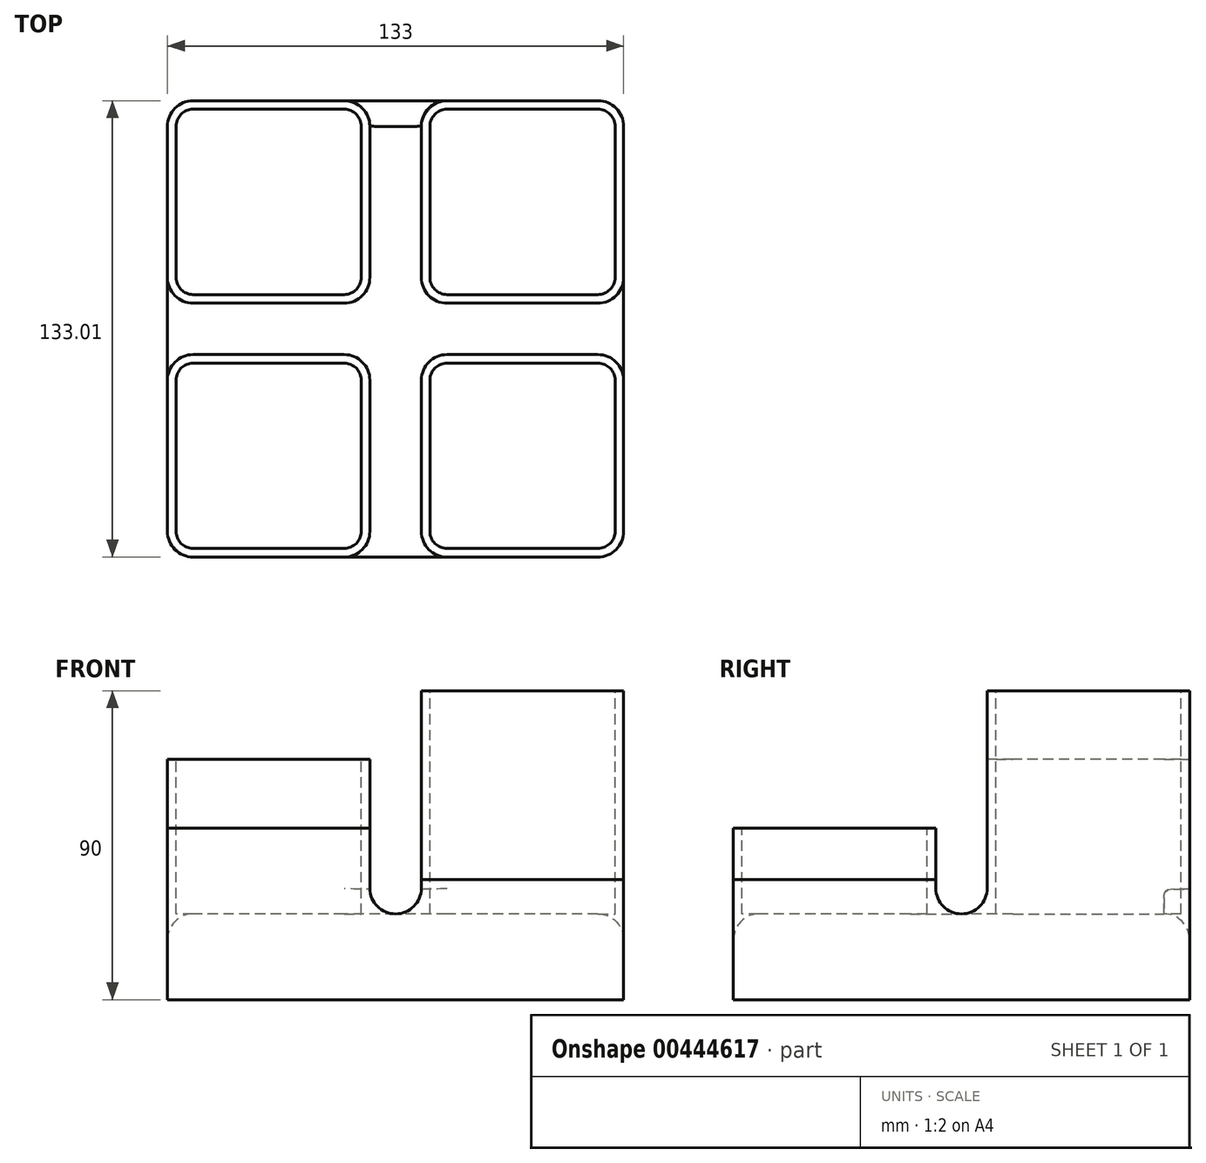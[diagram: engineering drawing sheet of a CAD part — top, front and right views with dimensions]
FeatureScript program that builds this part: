
annotation { "Feature Type Name" : "Feature", "Feature Type Description" : "" }
export const myFeature = defineFeature(function(context is Context, id is Id, definition is map)
    precondition{}
    {
        {
            var Q0;
            Q0=qCreatedBy(makeId("Top.planeOp"),FACE);
            var sketch = newSketch(context, id + "F0", { "sketchPlane" : qUnion([Q0])});
            skLineSegment(sketch, "E0", {"start": v(-66.5, 59) * mm, "end": v(-66.5, 15) * mm});
            skLineSegment(sketch, "E1", {"start": v(-15, -66.5) * mm, "end": v(-59, -66.5) * mm});
            skLineSegment(sketch, "E2", {"start": v(-66.5, -59) * mm, "end": v(-66.5, -15) * mm});
            skLineSegment(sketch, "E3", {"start": v(59, -66.5) * mm, "end": v(15, -66.5) * mm});
            skLineSegment(sketch, "E4", {"start": v(-59, -7.5) * mm, "end": v(-15, -7.5) * mm});
            skLineSegment(sketch, "E5", {"start": v(-7.5, -15) * mm, "end": v(-7.5, -59) * mm});
            skLineSegment(sketch, "E6", {"start": v(-59, 66.5) * mm, "end": v(-15, 66.5) * mm});
            skLineSegment(sketch, "E7", {"start": v(-7.5, 59) * mm, "end": v(-7.5, 15) * mm});
            skLineSegment(sketch, "E8", {"start": v(-15, 7.5) * mm, "end": v(-59, 7.5) * mm});
            skLineSegment(sketch, "E9", {"start": v(66.5, 59) * mm, "end": v(66.5, 15) * mm});
            skLineSegment(sketch, "E10", {"start": v(59, 7.5) * mm, "end": v(15, 7.5) * mm});
            skLineSegment(sketch, "E11", {"start": v(7.5, 15) * mm, "end": v(7.5, 59) * mm});
            skLineSegment(sketch, "E12", {"start": v(15, 66.5) * mm, "end": v(59, 66.5) * mm});
            skLineSegment(sketch, "E13", {"start": v(66.5, -59) * mm, "end": v(66.5, -15) * mm});
            skLineSegment(sketch, "E14", {"start": v(59, -7.5) * mm, "end": v(15, -7.5) * mm});
            skLineSegment(sketch, "E15", {"start": v(7.5, -15) * mm, "end": v(7.5, -59) * mm});
            skPoint(sketch, "E16.visualSharp", {"position": v(-64, 64) * mm});
            skPoint(sketch, "E17.visualSharp", {"position": v(-66.5, 66.5) * mm});
            skArc(sketch, "E17.filletArc", {"start": v(-59, 66.5) * mm, "mid": v(-64.3, 64.3) * mm, "end": v(-66.5, 59) * mm});
            skPoint(sketch, "E18.visualSharp", {"position": v(-64, 10) * mm});
            skPoint(sketch, "E19.newPointB", {"position": v(-66.5, 7.5) * mm});
            skArc(sketch, "E19.filletArc", {"start": v(-66.5, 15) * mm, "mid": v(-64.3, 9.7) * mm, "end": v(-59, 7.5) * mm});
            skPoint(sketch, "E20.visualSharp", {"position": v(-7.5, 7.5) * mm});
            skArc(sketch, "E20.filletArc", {"start": v(-15, 7.5) * mm, "mid": v(-9.7, 9.7) * mm, "end": v(-7.5, 15) * mm});
            skPoint(sketch, "E21.visualSharp", {"position": v(-10, 10) * mm});
            skPoint(sketch, "E22.visualSharp", {"position": v(-10, 64) * mm});
            skPoint(sketch, "E23.visualSharp", {"position": v(-7.5, 66.5) * mm});
            skArc(sketch, "E23.filletArc", {"start": v(-7.5, 59) * mm, "mid": v(-9.7, 64.3) * mm, "end": v(-15, 66.5) * mm});
            skPoint(sketch, "E24.visualSharp", {"position": v(10, 64) * mm});
            skPoint(sketch, "E25.visualSharp", {"position": v(7.5, 66.5) * mm});
            skArc(sketch, "E25.filletArc", {"start": v(15, 66.5) * mm, "mid": v(9.7, 64.3) * mm, "end": v(7.5, 59) * mm});
            skPoint(sketch, "E26.visualSharp", {"position": v(66.5, 66.5) * mm});
            skArc(sketch, "E26.filletArc", {"start": v(66.5, 59) * mm, "mid": v(64.3, 64.3) * mm, "end": v(59, 66.5) * mm});
            skPoint(sketch, "E27.visualSharp", {"position": v(64, 64) * mm});
            skPoint(sketch, "E28.visualSharp", {"position": v(66.5, -7.5) * mm});
            skArc(sketch, "E28.filletArc", {"start": v(66.5, -15) * mm, "mid": v(64.3, -9.7) * mm, "end": v(59, -7.5) * mm});
            skPoint(sketch, "E29.visualSharp", {"position": v(64, -10) * mm});
            skPoint(sketch, "E30.visualSharp", {"position": v(10, -10) * mm});
            skPoint(sketch, "E31.visualSharp", {"position": v(7.5, -7.5) * mm});
            skArc(sketch, "E31.filletArc", {"start": v(15, -7.5) * mm, "mid": v(9.7, -9.7) * mm, "end": v(7.5, -15) * mm});
            skPoint(sketch, "E32.visualSharp", {"position": v(10, -64) * mm});
            skArc(sketch, "E33.filletArc", {"start": v(7.5, -59) * mm, "mid": v(9.7, -64.3) * mm, "end": v(15, -66.5) * mm});
            skPoint(sketch, "E34.visualSharp", {"position": v(64, -64) * mm});
            skPoint(sketch, "E35.visualSharp", {"position": v(66.5, -66.5) * mm});
            skArc(sketch, "E35.filletArc", {"start": v(59, -66.5) * mm, "mid": v(64.3, -64.3) * mm, "end": v(66.5, -59) * mm});
            skPoint(sketch, "E36.visualSharp", {"position": v(10, 10) * mm});
            skPoint(sketch, "E37.visualSharp", {"position": v(7.5, 7.5) * mm});
            skArc(sketch, "E37.filletArc", {"start": v(7.5, 15) * mm, "mid": v(9.7, 9.7) * mm, "end": v(15, 7.5) * mm});
            skPoint(sketch, "E38.visualSharp", {"position": v(64, 10) * mm});
            skArc(sketch, "E39.filletArc", {"start": v(59, 7.5) * mm, "mid": v(64.3, 9.7) * mm, "end": v(66.5, 15) * mm});
            skPoint(sketch, "E40.visualSharp", {"position": v(-64, -10) * mm});
            skArc(sketch, "E41.filletArc", {"start": v(-59, -7.5) * mm, "mid": v(-64.3, -9.7) * mm, "end": v(-66.5, -15) * mm});
            skPoint(sketch, "E42.visualSharp", {"position": v(-64, -64) * mm});
            skPoint(sketch, "E43.visualSharp", {"position": v(-66.5, -66.5) * mm});
            skArc(sketch, "E43.filletArc", {"start": v(-66.5, -59) * mm, "mid": v(-64.3, -64.3) * mm, "end": v(-59, -66.5) * mm});
            skPoint(sketch, "E44.visualSharp", {"position": v(-7.5, -7.5) * mm});
            skArc(sketch, "E44.filletArc", {"start": v(-7.5, -15) * mm, "mid": v(-9.7, -9.7) * mm, "end": v(-15, -7.5) * mm});
            skPoint(sketch, "E45.visualSharp", {"position": v(-10, -10) * mm});
            skPoint(sketch, "E46.visualSharp", {"position": v(-10, -64) * mm});
            skPoint(sketch, "E47.visualSharp", {"position": v(-7.5, -66.5) * mm});
            skArc(sketch, "E47.filletArc", {"start": v(-15, -66.5) * mm, "mid": v(-9.7, -64.3) * mm, "end": v(-7.5, -59) * mm});
            skPoint(sketch, "E48.trimOffspring.end.orphan", {"position": v(-66.5, 0) * mm});
            skPoint(sketch, "E49.orphan", {"position": v(66.5, 7.5) * mm});
            skSolve(sketch);
        }
        {
            var Q0;
            Q0=makeQuery(id+"F0.imprint","IMPRINT",FACE,{"disambiguationData":[TD([[makeQuery(id+"F0.imprint","IMPRINT",EDGE,{"derivedFrom":sQuery(id+"F0.wireOp",EDGE,"E0")}),1.0]])]});
            extrude(context, id + "F1", {"entities" : qUnion([Q0]), "depth" : 70 * mm});
        }
        {
            var Q0;
            Q0=makeQuery(id+"F0.imprint","IMPRINT",FACE,{"disambiguationData":[TD([[makeQuery(id+"F0.imprint","IMPRINT",EDGE,{"derivedFrom":sQuery(id+"F0.wireOp",EDGE,"E9")}),-1.0]])]});
            extrude(context, id + "F2", {"entities" : qUnion([Q0]), "depth" : 90 * mm});
        }
        {
            var Q0;
            Q0=makeQuery(id+"F0.imprint","IMPRINT",FACE,{"disambiguationData":[TD([[makeQuery(id+"F0.imprint","IMPRINT",EDGE,{"derivedFrom":sQuery(id+"F0.wireOp",EDGE,"E2")}),-1.0]])]});
            extrude(context, id + "F3", {"entities" : qUnion([Q0]), "depth" : 50 * mm});
        }
        {
            var Q0;
            Q0=makeQuery(id+"F0.imprint","IMPRINT",FACE,{"disambiguationData":[TD([[makeQuery(id+"F0.imprint","IMPRINT",EDGE,{"derivedFrom":sQuery(id+"F0.wireOp",EDGE,"E3")}),-1.0]])]});
            extrude(context, id + "F4", {"entities" : qUnion([Q0]), "depth" : 35 * mm});
        }
        {
            var Q0;
            Q0=makeQuery(id+"F1.opExtrude","CAP_FACE",FACE,{"disambiguationData":[OSD([sQuery(id+"F0.wireOp",EDGE,"E0"),sQuery(id+"F0.wireOp",EDGE,"E6"),sQuery(id+"F0.wireOp",EDGE,"E7"),sQuery(id+"F0.wireOp",EDGE,"E8"),sQuery(id+"F0.wireOp",EDGE,"E17.filletArc"),sQuery(id+"F0.wireOp",EDGE,"E19.filletArc"),sQuery(id+"F0.wireOp",EDGE,"E20.filletArc"),sQuery(id+"F0.wireOp",EDGE,"E23.filletArc")])],"isStart":false});
            var sketch = newSketch(context, id + "F5", { "sketchPlane" : qUnion([Q0])});
            skArc(sketch, "E50.0", {"start": v(-59, 64) * mm, "mid": v(-62.54, 62.54) * mm, "end": v(-64, 59) * mm});
            skLineSegment(sketch, "E50.1", {"start": v(-64, 59) * mm, "end": v(-64, 15) * mm});
            skLineSegment(sketch, "E50.2", {"start": v(-59, 64) * mm, "end": v(-15, 64) * mm});
            skArc(sketch, "E50.3", {"start": v(-64, 15) * mm, "mid": v(-62.54, 11.46) * mm, "end": v(-59, 10) * mm});
            skArc(sketch, "E50.4", {"start": v(-10, 59) * mm, "mid": v(-11.46, 62.54) * mm, "end": v(-15, 64) * mm});
            skLineSegment(sketch, "E50.5", {"start": v(-10, 59) * mm, "end": v(-10, 15) * mm});
            skArc(sketch, "E50.6", {"start": v(-15, 10) * mm, "mid": v(-11.46, 11.46) * mm, "end": v(-10, 15) * mm});
            skLineSegment(sketch, "E50.7", {"start": v(-15, 10) * mm, "end": v(-59, 10) * mm});
            skSolve(sketch);
        }
        {
            var Q0;
            Q0=makeQuery(id+"F5.imprint","IMPRINT",FACE,{"disambiguationData":[TD([[makeQuery(id+"F5.imprint","IMPRINT",EDGE,{"derivedFrom":sQuery(id+"F5.wireOp",EDGE,"E50.0")}),1.0]])]});
            extrude(context, id + "F6", {"entities" : qUnion([Q0]), "operationType" : NewBodyOperationType.REMOVE, "endBound" : BoundingType.THROUGH_ALL, "oppositeDirection" : true, "depth" : 25 * mm});
        }
        {
            var Q0;
            Q0=makeQuery(id+"F2.opExtrude","CAP_FACE",FACE,{"disambiguationData":[OSD([sQuery(id+"F0.wireOp",EDGE,"E9"),sQuery(id+"F0.wireOp",EDGE,"E10"),sQuery(id+"F0.wireOp",EDGE,"E11"),sQuery(id+"F0.wireOp",EDGE,"E12"),sQuery(id+"F0.wireOp",EDGE,"E25.filletArc"),sQuery(id+"F0.wireOp",EDGE,"E26.filletArc"),sQuery(id+"F0.wireOp",EDGE,"E37.filletArc"),sQuery(id+"F0.wireOp",EDGE,"E39.filletArc")])],"isStart":false});
            var sketch = newSketch(context, id + "F7", { "sketchPlane" : qUnion([Q0])});
            skArc(sketch, "E51.0", {"start": v(15, 64) * mm, "mid": v(11.46, 62.54) * mm, "end": v(10, 59) * mm});
            skLineSegment(sketch, "E51.1", {"start": v(10, 15) * mm, "end": v(10, 59) * mm});
            skLineSegment(sketch, "E51.2", {"start": v(15, 64) * mm, "end": v(59, 64) * mm});
            skArc(sketch, "E51.3", {"start": v(10, 15) * mm, "mid": v(11.46, 11.46) * mm, "end": v(15, 10) * mm});
            skArc(sketch, "E51.4", {"start": v(64, 59) * mm, "mid": v(62.54, 62.54) * mm, "end": v(59, 64) * mm});
            skLineSegment(sketch, "E51.5", {"start": v(64, 59) * mm, "end": v(64, 15) * mm});
            skArc(sketch, "E51.6", {"start": v(59, 10) * mm, "mid": v(62.54, 11.46) * mm, "end": v(64, 15) * mm});
            skLineSegment(sketch, "E51.7", {"start": v(59, 10) * mm, "end": v(15, 10) * mm});
            skSolve(sketch);
        }
        {
            var Q0;
            Q0=makeQuery(id+"F7.imprint","IMPRINT",FACE,{"disambiguationData":[TD([[makeQuery(id+"F7.imprint","IMPRINT",EDGE,{"derivedFrom":sQuery(id+"F7.wireOp",EDGE,"E51.0")}),1.0]])]});
            extrude(context, id + "F8", {"entities" : qUnion([Q0]), "operationType" : NewBodyOperationType.REMOVE, "endBound" : BoundingType.THROUGH_ALL, "oppositeDirection" : true, "depth" : 25 * mm});
        }
        {
            var Q0;
            Q0=makeQuery(id+"F3.opExtrude","CAP_FACE",FACE,{"disambiguationData":[OSD([sQuery(id+"F0.wireOp",EDGE,"E2"),sQuery(id+"F0.wireOp",EDGE,"E4"),sQuery(id+"F0.wireOp",EDGE,"E5"),sQuery(id+"F0.wireOp",EDGE,"E1"),sQuery(id+"F0.wireOp",EDGE,"E41.filletArc"),sQuery(id+"F0.wireOp",EDGE,"E43.filletArc"),sQuery(id+"F0.wireOp",EDGE,"E44.filletArc"),sQuery(id+"F0.wireOp",EDGE,"E47.filletArc")])],"isStart":false});
            var sketch = newSketch(context, id + "F9", { "sketchPlane" : qUnion([Q0])});
            skArc(sketch, "E52.0", {"start": v(-59, -10) * mm, "mid": v(-62.54, -11.46) * mm, "end": v(-64, -15) * mm});
            skLineSegment(sketch, "E52.1", {"start": v(-64, -59) * mm, "end": v(-64, -15) * mm});
            skLineSegment(sketch, "E52.2", {"start": v(-59, -10) * mm, "end": v(-15, -10) * mm});
            skArc(sketch, "E52.3", {"start": v(-64, -59) * mm, "mid": v(-62.54, -62.54) * mm, "end": v(-59, -64) * mm});
            skArc(sketch, "E52.4", {"start": v(-10, -15) * mm, "mid": v(-11.46, -11.46) * mm, "end": v(-15, -10) * mm});
            skLineSegment(sketch, "E52.5", {"start": v(-10, -15) * mm, "end": v(-10, -59) * mm});
            skArc(sketch, "E52.6", {"start": v(-15, -64) * mm, "mid": v(-11.46, -62.54) * mm, "end": v(-10, -59) * mm});
            skLineSegment(sketch, "E52.7", {"start": v(-15, -64) * mm, "end": v(-59, -64) * mm});
            skSolve(sketch);
        }
        {
            var Q0;
            Q0=makeQuery(id+"F9.imprint","IMPRINT",FACE,{"disambiguationData":[TD([[makeQuery(id+"F9.imprint","IMPRINT",EDGE,{"derivedFrom":sQuery(id+"F9.wireOp",EDGE,"E52.0")}),1.0]])]});
            extrude(context, id + "F10", {"entities" : qUnion([Q0]), "operationType" : NewBodyOperationType.REMOVE, "endBound" : BoundingType.THROUGH_ALL, "oppositeDirection" : true, "depth" : 25 * mm});
        }
        {
            var Q0;
            Q0=makeQuery(id+"F4.opExtrude","CAP_FACE",FACE,{"disambiguationData":[OSD([sQuery(id+"F0.wireOp",EDGE,"E3"),sQuery(id+"F0.wireOp",EDGE,"E13"),sQuery(id+"F0.wireOp",EDGE,"E14"),sQuery(id+"F0.wireOp",EDGE,"E15"),sQuery(id+"F0.wireOp",EDGE,"E28.filletArc"),sQuery(id+"F0.wireOp",EDGE,"E31.filletArc"),sQuery(id+"F0.wireOp",EDGE,"E33.filletArc"),sQuery(id+"F0.wireOp",EDGE,"E35.filletArc")])],"isStart":false});
            var sketch = newSketch(context, id + "F11", { "sketchPlane" : qUnion([Q0])});
            skArc(sketch, "E53.0", {"start": v(64, -15) * mm, "mid": v(62.54, -11.46) * mm, "end": v(59, -10) * mm});
            skLineSegment(sketch, "E53.1", {"start": v(64, -59) * mm, "end": v(64, -15) * mm});
            skLineSegment(sketch, "E53.2", {"start": v(59, -10) * mm, "end": v(15, -10) * mm});
            skArc(sketch, "E53.3", {"start": v(59, -64) * mm, "mid": v(62.54, -62.54) * mm, "end": v(64, -59) * mm});
            skArc(sketch, "E53.4", {"start": v(15, -10) * mm, "mid": v(11.46, -11.46) * mm, "end": v(10, -15) * mm});
            skLineSegment(sketch, "E53.5", {"start": v(10, -15) * mm, "end": v(10, -59) * mm});
            skArc(sketch, "E53.6", {"start": v(10, -59) * mm, "mid": v(11.46, -62.54) * mm, "end": v(15, -64) * mm});
            skLineSegment(sketch, "E53.7", {"start": v(59, -64) * mm, "end": v(15, -64) * mm});
            skSolve(sketch);
        }
        {
            var Q0;
            Q0=makeQuery(id+"F11.imprint","IMPRINT",FACE,{"disambiguationData":[TD([[makeQuery(id+"F11.imprint","IMPRINT",EDGE,{"derivedFrom":sQuery(id+"F11.wireOp",EDGE,"E53.0")}),1.0]])]});
            extrude(context, id + "F12", {"entities" : qUnion([Q0]), "operationType" : NewBodyOperationType.REMOVE, "endBound" : BoundingType.THROUGH_ALL, "oppositeDirection" : true, "depth" : 25 * mm});
        }
        {
            var Q0;
            Q0=qCreatedBy(makeId("Top.planeOp"),FACE);
            var sketch = newSketch(context, id + "F13", { "sketchPlane" : qUnion([Q0])});
            skLineSegment(sketch, "E54", {"start": v(0, 0) * mm, "end": v(0, 66.5) * mm});
            skLineSegment(sketch, "E55", {"start": v(0, 0) * mm, "end": v(0, -66.5) * mm});
            skLineSegment(sketch, "E56", {"start": v(0, 0) * mm, "end": v(-66.5, 0) * mm});
            skLineSegment(sketch, "E57", {"start": v(0, 0) * mm, "end": v(66.5, 0) * mm});
            skLineSegment(sketch, "E58", {"start": v(0, 66.5) * mm, "end": v(59, 66.5) * mm});
            skLineSegment(sketch, "E59", {"start": v(66.5, 59) * mm, "end": v(66.5, 0) * mm});
            skLineSegment(sketch, "E60", {"start": v(0, 66.5) * mm, "end": v(-59, 66.5) * mm});
            skLineSegment(sketch, "E61", {"start": v(-66.5, 59) * mm, "end": v(-66.5, 0) * mm});
            skLineSegment(sketch, "E62", {"start": v(-66.5, 0) * mm, "end": v(-66.5, -59) * mm});
            skLineSegment(sketch, "E63", {"start": v(-59, -66.5) * mm, "end": v(0, -66.5) * mm});
            skLineSegment(sketch, "E64", {"start": v(0, -66.5) * mm, "end": v(59, -66.5) * mm});
            skLineSegment(sketch, "E65", {"start": v(66.5, -59) * mm, "end": v(66.5, 0) * mm});
            skPoint(sketch, "E66.visualSharp", {"position": v(-66.5, 66.5) * mm});
            skArc(sketch, "E66.filletArc", {"start": v(-59, 66.5) * mm, "mid": v(-64.3, 64.3) * mm, "end": v(-66.5, 59) * mm});
            skPoint(sketch, "E67.visualSharp", {"position": v(66.5, 66.5) * mm});
            skArc(sketch, "E67.filletArc", {"start": v(66.5, 59) * mm, "mid": v(64.3, 64.3) * mm, "end": v(59, 66.5) * mm});
            skPoint(sketch, "E68.visualSharp", {"position": v(66.5, -66.5) * mm});
            skArc(sketch, "E68.filletArc", {"start": v(59, -66.5) * mm, "mid": v(64.3, -64.3) * mm, "end": v(66.5, -59) * mm});
            skPoint(sketch, "E69.visualSharp", {"position": v(-66.5, -66.5) * mm});
            skArc(sketch, "E69.filletArc", {"start": v(-66.5, -59) * mm, "mid": v(-64.3, -64.3) * mm, "end": v(-59, -66.5) * mm});
            skSolve(sketch);
        }
        {
            var Q0;
            Q0=makeQuery(id+"F13.imprint","IMPRINT",FACE,{"disambiguationData":[TD([[makeQuery(id+"F13.imprint","IMPRINT",EDGE,{"derivedFrom":sQuery(id+"F13.wireOp",EDGE,"E54")}),-1.0]])]});
            var Q1;
            Q1=makeQuery(id+"F13.imprint","IMPRINT",FACE,{"disambiguationData":[TD([[makeQuery(id+"F13.imprint","IMPRINT",EDGE,{"derivedFrom":sQuery(id+"F13.wireOp",EDGE,"E55")}),-1.0]])]});
            var Q2;
            Q2=makeQuery(id+"F13.imprint","IMPRINT",FACE,{"disambiguationData":[TD([[makeQuery(id+"F13.imprint","IMPRINT",EDGE,{"derivedFrom":sQuery(id+"F13.wireOp",EDGE,"E55")}),1.0]])]});
            var Q3;
            Q3=makeQuery(id+"F13.imprint","IMPRINT",FACE,{"disambiguationData":[TD([[makeQuery(id+"F13.imprint","IMPRINT",EDGE,{"derivedFrom":sQuery(id+"F13.wireOp",EDGE,"E54")}),1.0]])]});
            extrude(context, id + "F14", {"entities" : qUnion([Q0, Q1, Q2, Q3]), "operationType" : NewBodyOperationType.ADD, "depth" : 25 * mm});
        }
        {
            var Q0;
            Q0=makeQuery(id+"F14.boolean.opBoolean","INTERSECT",EDGE,{"derivedFrom":[makeQuery(id+"F3.opExtrude","SWEPT_FACE",FACE,{"disambiguationData":[OSD([sQuery(id+"F0.wireOp",EDGE,"E5")])]}),makeQuery(id+"F14.opExtrude","CAP_FACE",FACE,{"disambiguationData":[OSD([sQuery(id+"F13.wireOp",EDGE,"E58"),sQuery(id+"F13.wireOp",EDGE,"E59"),sQuery(id+"F13.wireOp",EDGE,"E60"),sQuery(id+"F13.wireOp",EDGE,"E61"),sQuery(id+"F13.wireOp",EDGE,"E62"),sQuery(id+"F13.wireOp",EDGE,"E63"),sQuery(id+"F13.wireOp",EDGE,"E64"),sQuery(id+"F13.wireOp",EDGE,"E65"),sQuery(id+"F13.wireOp",EDGE,"E66.filletArc"),sQuery(id+"F13.wireOp",EDGE,"E67.filletArc"),sQuery(id+"F13.wireOp",EDGE,"E68.filletArc"),sQuery(id+"F13.wireOp",EDGE,"E69.filletArc")])],"isStart":false})]});
            fillet(context, id + "F15", {"entities" : qUnion([Q0]), "radius" : 7.5 * mm, "tangentPropagation" : true, "allowEdgeOverflow" : false});
        }
        {
            var Q0;
            Q0=makeQuery(id+"F14.boolean.opBoolean","INTERSECT",EDGE,{"derivedFrom":[makeQuery(id+"F1.opExtrude","SWEPT_FACE",FACE,{"disambiguationData":[OSD([sQuery(id+"F0.wireOp",EDGE,"E8")])]}),makeQuery(id+"F14.opExtrude","CAP_FACE",FACE,{"disambiguationData":[OSD([sQuery(id+"F13.wireOp",EDGE,"E58"),sQuery(id+"F13.wireOp",EDGE,"E59"),sQuery(id+"F13.wireOp",EDGE,"E60"),sQuery(id+"F13.wireOp",EDGE,"E61"),sQuery(id+"F13.wireOp",EDGE,"E62"),sQuery(id+"F13.wireOp",EDGE,"E63"),sQuery(id+"F13.wireOp",EDGE,"E64"),sQuery(id+"F13.wireOp",EDGE,"E65"),sQuery(id+"F13.wireOp",EDGE,"E66.filletArc"),sQuery(id+"F13.wireOp",EDGE,"E67.filletArc"),sQuery(id+"F13.wireOp",EDGE,"E68.filletArc"),sQuery(id+"F13.wireOp",EDGE,"E69.filletArc")])],"isStart":false})]});
            fillet(context, id + "F16", {"entities" : qUnion([Q0]), "radius" : 7.5 * mm, "tangentPropagation" : true, "allowEdgeOverflow" : false});
        }
        {
            var Q0;
            Q0=makeQuery(id+"F14.boolean.opBoolean","INTERSECT",EDGE,{"derivedFrom":[makeQuery(id+"F2.opExtrude","SWEPT_FACE",FACE,{"disambiguationData":[OSD([sQuery(id+"F0.wireOp",EDGE,"E11")])]}),makeQuery(id+"F14.opExtrude","CAP_FACE",FACE,{"disambiguationData":[OSD([sQuery(id+"F13.wireOp",EDGE,"E58"),sQuery(id+"F13.wireOp",EDGE,"E59"),sQuery(id+"F13.wireOp",EDGE,"E60"),sQuery(id+"F13.wireOp",EDGE,"E61"),sQuery(id+"F13.wireOp",EDGE,"E62"),sQuery(id+"F13.wireOp",EDGE,"E63"),sQuery(id+"F13.wireOp",EDGE,"E64"),sQuery(id+"F13.wireOp",EDGE,"E65"),sQuery(id+"F13.wireOp",EDGE,"E66.filletArc"),sQuery(id+"F13.wireOp",EDGE,"E67.filletArc"),sQuery(id+"F13.wireOp",EDGE,"E68.filletArc"),sQuery(id+"F13.wireOp",EDGE,"E69.filletArc")])],"isStart":false})]});
            fillet(context, id + "F17", {"entities" : qUnion([Q0]), "radius" : 7.5 * mm, "tangentPropagation" : true, "allowEdgeOverflow" : false});
        }
        {
            var Q0;
            Q0=makeQuery(id+"F14.boolean.opBoolean","INTERSECT",EDGE,{"derivedFrom":[makeQuery(id+"F4.opExtrude","SWEPT_FACE",FACE,{"disambiguationData":[OSD([sQuery(id+"F0.wireOp",EDGE,"E14")])]}),makeQuery(id+"F14.opExtrude","CAP_FACE",FACE,{"disambiguationData":[OSD([sQuery(id+"F13.wireOp",EDGE,"E58"),sQuery(id+"F13.wireOp",EDGE,"E59"),sQuery(id+"F13.wireOp",EDGE,"E60"),sQuery(id+"F13.wireOp",EDGE,"E61"),sQuery(id+"F13.wireOp",EDGE,"E62"),sQuery(id+"F13.wireOp",EDGE,"E63"),sQuery(id+"F13.wireOp",EDGE,"E64"),sQuery(id+"F13.wireOp",EDGE,"E65"),sQuery(id+"F13.wireOp",EDGE,"E66.filletArc"),sQuery(id+"F13.wireOp",EDGE,"E67.filletArc"),sQuery(id+"F13.wireOp",EDGE,"E68.filletArc"),sQuery(id+"F13.wireOp",EDGE,"E69.filletArc")])],"isStart":false})]});
            fillet(context, id + "F18", {"entities" : qUnion([Q0]), "radius" : 7.5 * mm, "tangentPropagation" : true, "allowEdgeOverflow" : false});
        }
        {
            var Q0;
            {var subQ0=sQuery(id+"F13.wireOp",EDGE,"E64");var subQ1=sQuery(id+"F13.wireOp",EDGE,"E63");Q0=makeQuery(id+"F15.opFillet","BLEND_EDGE",EDGE,{"blendedFrom":[makeQuery(id+"F14.boolean.opBoolean","INTERSECT",EDGE,{"derivedFrom":[makeQuery(id+"F3.opExtrude","SWEPT_FACE",FACE,{"disambiguationData":[OSD([sQuery(id+"F0.wireOp",EDGE,"E47.filletArc")])]}),makeQuery(id+"F14.opExtrude","CAP_FACE",FACE,{"disambiguationData":[OSD([sQuery(id+"F13.wireOp",EDGE,"E58"),sQuery(id+"F13.wireOp",EDGE,"E59"),sQuery(id+"F13.wireOp",EDGE,"E60"),sQuery(id+"F13.wireOp",EDGE,"E61"),sQuery(id+"F13.wireOp",EDGE,"E62"),subQ1,subQ0,sQuery(id+"F13.wireOp",EDGE,"E65"),sQuery(id+"F13.wireOp",EDGE,"E66.filletArc"),sQuery(id+"F13.wireOp",EDGE,"E67.filletArc"),sQuery(id+"F13.wireOp",EDGE,"E68.filletArc"),sQuery(id+"F13.wireOp",EDGE,"E69.filletArc")])],"isStart":false})]}),makeQuery(id+"F14.boolean.opBoolean","MERGE",FACE,{"derivedFrom":[makeQuery(id+"F3.opExtrude","SWEPT_FACE",FACE,{"disambiguationData":[OSD([sQuery(id+"F0.wireOp",EDGE,"E1")])]}),makeQuery(id+"F4.opExtrude","SWEPT_FACE",FACE,{"disambiguationData":[OSD([sQuery(id+"F0.wireOp",EDGE,"E3")])]}),makeQuery(id+"F14.opExtrude","SWEPT_FACE",FACE,{"disambiguationData":[OSD([subQ1,subQ0])]})]})],"blendedInto":[makeQuery(id+"F14.boolean.opBoolean","MERGE",FACE,{"derivedFrom":[makeQuery(id+"F3.opExtrude","SWEPT_FACE",FACE,{"disambiguationData":[OSD([sQuery(id+"F0.wireOp",EDGE,"E1")])]}),makeQuery(id+"F4.opExtrude","SWEPT_FACE",FACE,{"disambiguationData":[OSD([sQuery(id+"F0.wireOp",EDGE,"E3")])]}),makeQuery(id+"F14.opExtrude","SWEPT_FACE",FACE,{"disambiguationData":[OSD([subQ1,subQ0])]})]})]});}
            fillet(context, id + "F19", {"entities" : qUnion([Q0]), "radius" : 7.5 * mm, "tangentPropagation" : true, "allowEdgeOverflow" : false});
        }
        {
            var Q0;
            {var subQ0=sQuery(id+"F13.wireOp",EDGE,"E65");var subQ1=sQuery(id+"F13.wireOp",EDGE,"E59");Q0=makeQuery(id+"F18.opFillet","BLEND_EDGE",EDGE,{"blendedFrom":[makeQuery(id+"F14.boolean.opBoolean","INTERSECT",EDGE,{"derivedFrom":[makeQuery(id+"F4.opExtrude","SWEPT_FACE",FACE,{"disambiguationData":[OSD([sQuery(id+"F0.wireOp",EDGE,"E28.filletArc")])]}),makeQuery(id+"F14.opExtrude","CAP_FACE",FACE,{"disambiguationData":[OSD([sQuery(id+"F13.wireOp",EDGE,"E58"),subQ1,sQuery(id+"F13.wireOp",EDGE,"E60"),sQuery(id+"F13.wireOp",EDGE,"E61"),sQuery(id+"F13.wireOp",EDGE,"E62"),sQuery(id+"F13.wireOp",EDGE,"E63"),sQuery(id+"F13.wireOp",EDGE,"E64"),subQ0,sQuery(id+"F13.wireOp",EDGE,"E66.filletArc"),sQuery(id+"F13.wireOp",EDGE,"E67.filletArc"),sQuery(id+"F13.wireOp",EDGE,"E68.filletArc"),sQuery(id+"F13.wireOp",EDGE,"E69.filletArc")])],"isStart":false})]}),makeQuery(id+"F14.boolean.opBoolean","MERGE",FACE,{"derivedFrom":[makeQuery(id+"F2.opExtrude","SWEPT_FACE",FACE,{"disambiguationData":[OSD([sQuery(id+"F0.wireOp",EDGE,"E9")])]}),makeQuery(id+"F4.opExtrude","SWEPT_FACE",FACE,{"disambiguationData":[OSD([sQuery(id+"F0.wireOp",EDGE,"E13")])]}),makeQuery(id+"F14.opExtrude","SWEPT_FACE",FACE,{"disambiguationData":[OSD([subQ1,subQ0])]})]})],"blendedInto":[makeQuery(id+"F14.boolean.opBoolean","MERGE",FACE,{"derivedFrom":[makeQuery(id+"F2.opExtrude","SWEPT_FACE",FACE,{"disambiguationData":[OSD([sQuery(id+"F0.wireOp",EDGE,"E9")])]}),makeQuery(id+"F4.opExtrude","SWEPT_FACE",FACE,{"disambiguationData":[OSD([sQuery(id+"F0.wireOp",EDGE,"E13")])]}),makeQuery(id+"F14.opExtrude","SWEPT_FACE",FACE,{"disambiguationData":[OSD([subQ1,subQ0])]})]})]});}
            fillet(context, id + "F20", {"entities" : qUnion([Q0]), "radius" : 7.5 * mm, "tangentPropagation" : true, "allowEdgeOverflow" : false});
        }
        {
            var Q0;
            {var subQ0=sQuery(id+"F13.wireOp",EDGE,"E62");var subQ1=sQuery(id+"F13.wireOp",EDGE,"E61");Q0=makeQuery(id+"F16.opFillet","BLEND_EDGE",EDGE,{"blendedFrom":[makeQuery(id+"F14.boolean.opBoolean","INTERSECT",EDGE,{"derivedFrom":[makeQuery(id+"F1.opExtrude","SWEPT_FACE",FACE,{"disambiguationData":[OSD([sQuery(id+"F0.wireOp",EDGE,"E19.filletArc")])]}),makeQuery(id+"F14.opExtrude","CAP_FACE",FACE,{"disambiguationData":[OSD([sQuery(id+"F13.wireOp",EDGE,"E58"),sQuery(id+"F13.wireOp",EDGE,"E59"),sQuery(id+"F13.wireOp",EDGE,"E60"),subQ1,subQ0,sQuery(id+"F13.wireOp",EDGE,"E63"),sQuery(id+"F13.wireOp",EDGE,"E64"),sQuery(id+"F13.wireOp",EDGE,"E65"),sQuery(id+"F13.wireOp",EDGE,"E66.filletArc"),sQuery(id+"F13.wireOp",EDGE,"E67.filletArc"),sQuery(id+"F13.wireOp",EDGE,"E68.filletArc"),sQuery(id+"F13.wireOp",EDGE,"E69.filletArc")])],"isStart":false})]}),makeQuery(id+"F14.boolean.opBoolean","MERGE",FACE,{"derivedFrom":[makeQuery(id+"F1.opExtrude","SWEPT_FACE",FACE,{"disambiguationData":[OSD([sQuery(id+"F0.wireOp",EDGE,"E0")])]}),makeQuery(id+"F3.opExtrude","SWEPT_FACE",FACE,{"disambiguationData":[OSD([sQuery(id+"F0.wireOp",EDGE,"E2")])]}),makeQuery(id+"F14.opExtrude","SWEPT_FACE",FACE,{"disambiguationData":[OSD([subQ1,subQ0])]})]})],"blendedInto":[makeQuery(id+"F14.boolean.opBoolean","MERGE",FACE,{"derivedFrom":[makeQuery(id+"F1.opExtrude","SWEPT_FACE",FACE,{"disambiguationData":[OSD([sQuery(id+"F0.wireOp",EDGE,"E0")])]}),makeQuery(id+"F3.opExtrude","SWEPT_FACE",FACE,{"disambiguationData":[OSD([sQuery(id+"F0.wireOp",EDGE,"E2")])]}),makeQuery(id+"F14.opExtrude","SWEPT_FACE",FACE,{"disambiguationData":[OSD([subQ1,subQ0])]})]})]});}
            fillet(context, id + "F21", {"entities" : qUnion([Q0]), "radius" : 7.5 * mm, "tangentPropagation" : true, "allowEdgeOverflow" : false});
        }
        {
            var Q0;
            Q0=makeQuery(id+"F17.opFillet","BLEND_FACE",FACE,{"disambiguationData":[OSD([sQuery(id+"F0.wireOp",EDGE,"E25.filletArc"),sQuery(id+"F13.wireOp",EDGE,"E58"),sQuery(id+"F13.wireOp",EDGE,"E59"),sQuery(id+"F13.wireOp",EDGE,"E60"),sQuery(id+"F13.wireOp",EDGE,"E61"),sQuery(id+"F13.wireOp",EDGE,"E62"),sQuery(id+"F13.wireOp",EDGE,"E63"),sQuery(id+"F13.wireOp",EDGE,"E64"),sQuery(id+"F13.wireOp",EDGE,"E65"),sQuery(id+"F13.wireOp",EDGE,"E66.filletArc"),sQuery(id+"F13.wireOp",EDGE,"E67.filletArc"),sQuery(id+"F13.wireOp",EDGE,"E68.filletArc"),sQuery(id+"F13.wireOp",EDGE,"E69.filletArc")])]});
            fillet(context, id + "F22", {"entities" : qUnion([Q0]), "radius" : 7.5 * mm, "tangentPropagation" : true, "allowEdgeOverflow" : false});
        }
    });
